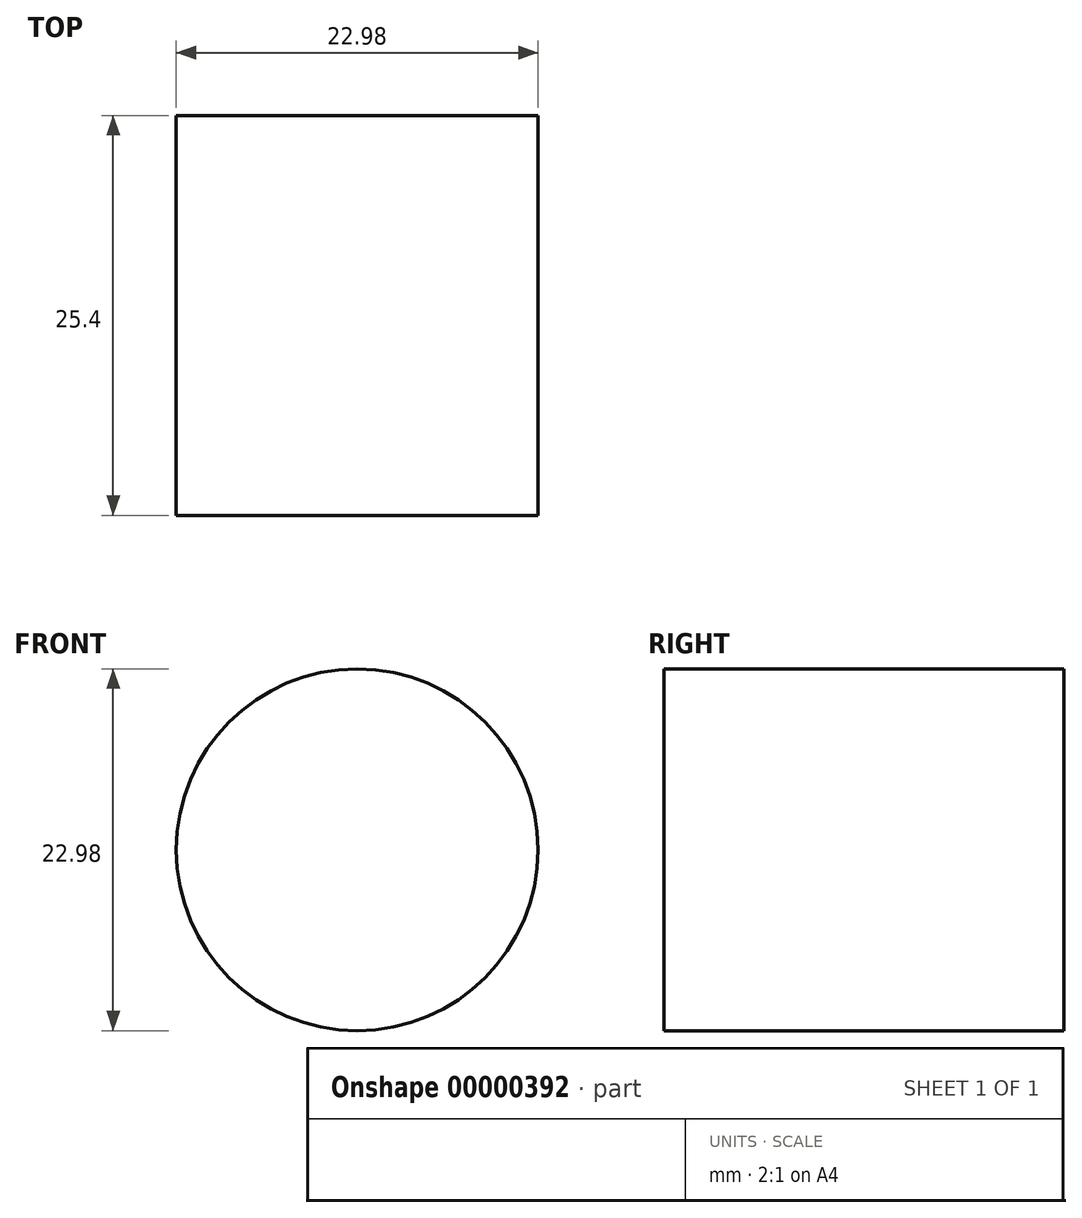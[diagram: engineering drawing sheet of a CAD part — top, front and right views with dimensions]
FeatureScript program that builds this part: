
annotation { "Feature Type Name" : "Feature", "Feature Type Description" : "" }
export const myFeature = defineFeature(function(context is Context, id is Id, definition is map)
    precondition{}
    {
        {
            var Q0;
            Q0=qCreatedBy(makeId("Front.planeOp"),FACE);
            var sketch = newSketch(context, id + "F0", { "sketchPlane" : qUnion([Q0])});
            skCircle(sketch, "E0", {"center": v(0, 0) * mm, "radius": 11.49 * mm});
            skSolve(sketch);
        }
        {
            var Q0;
            Q0=makeQuery(id+"F0.imprint","IMPRINT",FACE,{"disambiguationData":[TD([[makeQuery(id+"F0.imprint","IMPRINT",EDGE,{"derivedFrom":sQuery(id+"F0.wireOp",EDGE,"E0")}),1.0]])]});
            extrude(context, id + "F1", {"entities" : qUnion([Q0]), "depth" : 25.4 * mm});
        }
    });
